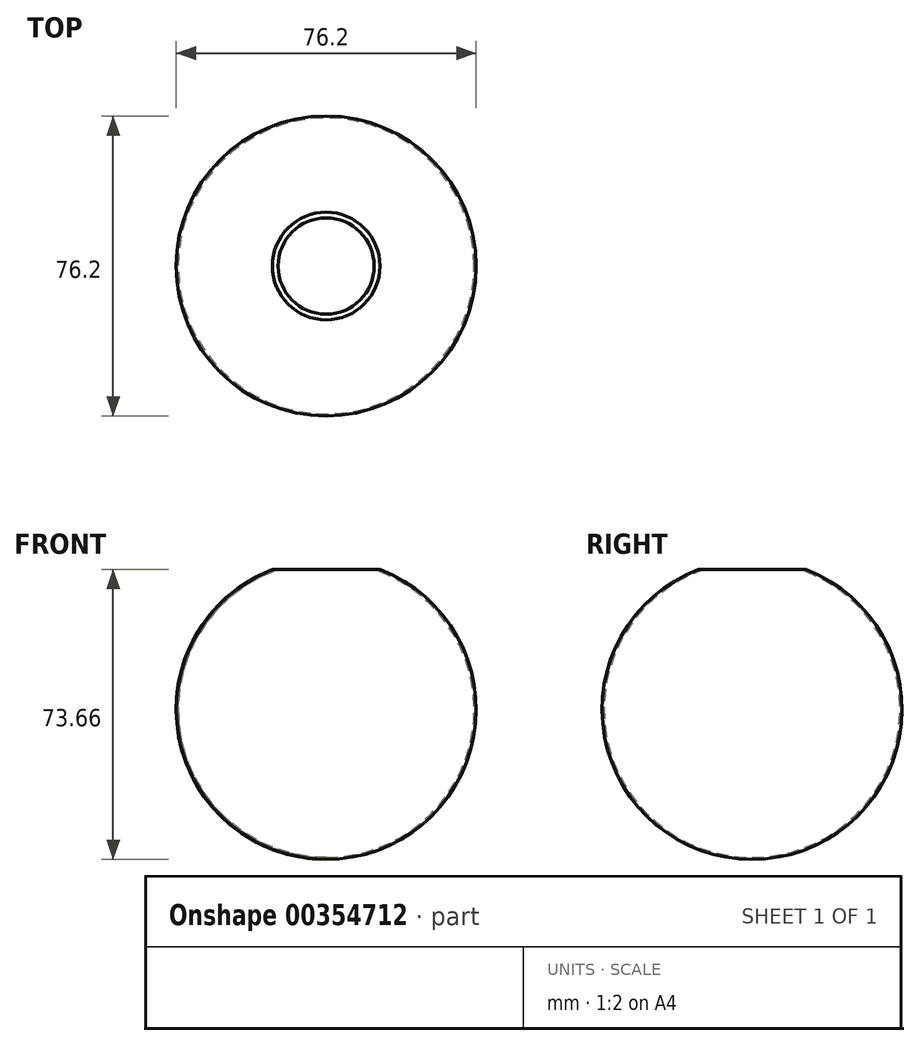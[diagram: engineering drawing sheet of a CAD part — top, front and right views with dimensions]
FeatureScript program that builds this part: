
annotation { "Feature Type Name" : "Feature", "Feature Type Description" : "" }
export const myFeature = defineFeature(function(context is Context, id is Id, definition is map)
    precondition{}
    {
        {
            var Q0;
            Q0=qCreatedBy(makeId("Front.planeOp"),FACE);
            var sketch = newSketch(context, id + "F0", { "sketchPlane" : qUnion([Q0])});
            skCircle(sketch, "E0", {"center": v(0, 0) * mm, "radius": 38.1 * mm});
            skLineSegment(sketch, "E1", {"start": v(0, 38.1) * mm, "end": v(0, -38.1) * mm});
            skSolve(sketch);
        }
        {
            var Q0;
            {var subQ0=sQuery(id+"F0.wireOp",EDGE,"E1");Q0=makeQuery(id+"F0.imprint","IMPRINT",FACE,{"disambiguationData":[TD([[makeQuery(id+"F0.imprint","IMPRINT",EDGE,{"derivedFrom":subQ0}),1.0]])]});}
            var Q1;
            Q1=sQuery(id+"F0.wireOp",EDGE,"E1");
            revolve(context, id + "F1", {"entities" : qUnion([Q0]), "axis" : qUnion([Q1]), "revolveType" : RevolveType.FULL});
        }
        {
            var Q0;
            Q0=qCreatedBy(makeId("Top.planeOp"),FACE);
            cPlane(context, id + "F2", {"entities" : qUnion([Q0]), "cplaneType" : CPlaneType.OFFSET, "offset" : 35.56 * mm, "width" : 152.4 * mm, "height" : 152.4 * mm});
        }
        {
            var Q0;
            Q0=qCreatedBy(id+"F2.planeOp",FACE);
            var sketch = newSketch(context, id + "F3", { "sketchPlane" : qUnion([Q0])});
            skLineSegment(sketch, "E2.bottom", {"start": v(-16.51, 16.51) * mm, "end": v(16.51, 16.51) * mm});
            skLineSegment(sketch, "E2.top", {"start": v(-16.51, -16.51) * mm, "end": v(16.51, -16.51) * mm});
            skLineSegment(sketch, "E2.left", {"start": v(-16.51, 16.51) * mm, "end": v(-16.51, -16.51) * mm});
            skLineSegment(sketch, "E2.right", {"start": v(16.51, 16.51) * mm, "end": v(16.51, -16.51) * mm});
            skPoint(sketch, "E2.middle", {"position": v(0, 0) * mm});
            skSolve(sketch);
        }
        {
            var Q0;
            Q0 = qSketchRegion(id + "F3", true);
            extrude(context, id + "F4", {"entities" : qUnion([Q0]), "operationType" : NewBodyOperationType.REMOVE, "depth" : 25.4 * mm});
        }
        {
            var Q0;
            Q0=makeQuery(id+"F4.boolean.opBoolean","COPY",FACE,{"derivedFrom":makeQuery(id+"F4.opExtrude","CAP_FACE",FACE,{"disambiguationData":[OSD([sQuery(id+"F3.wireOp",EDGE,"E2.bottom"),sQuery(id+"F3.wireOp",EDGE,"E2.top"),sQuery(id+"F3.wireOp",EDGE,"E2.left"),sQuery(id+"F3.wireOp",EDGE,"E2.right")])],"isStart":true})});
            shell(context, id + "F5", {"entities" : qUnion([Q0]), "thickness" : .5 * mm});
        }
        {
            var Q0;
            Q0=qCreatedBy(makeId("Front.planeOp"),FACE);
            cPlane(context, id + "F6", {"entities" : qUnion([Q0]), "cplaneType" : CPlaneType.OFFSET, "offset" : 41.9 * mm, "width" : 152.4 * mm, "height" : 152.4 * mm});
        }
    });
